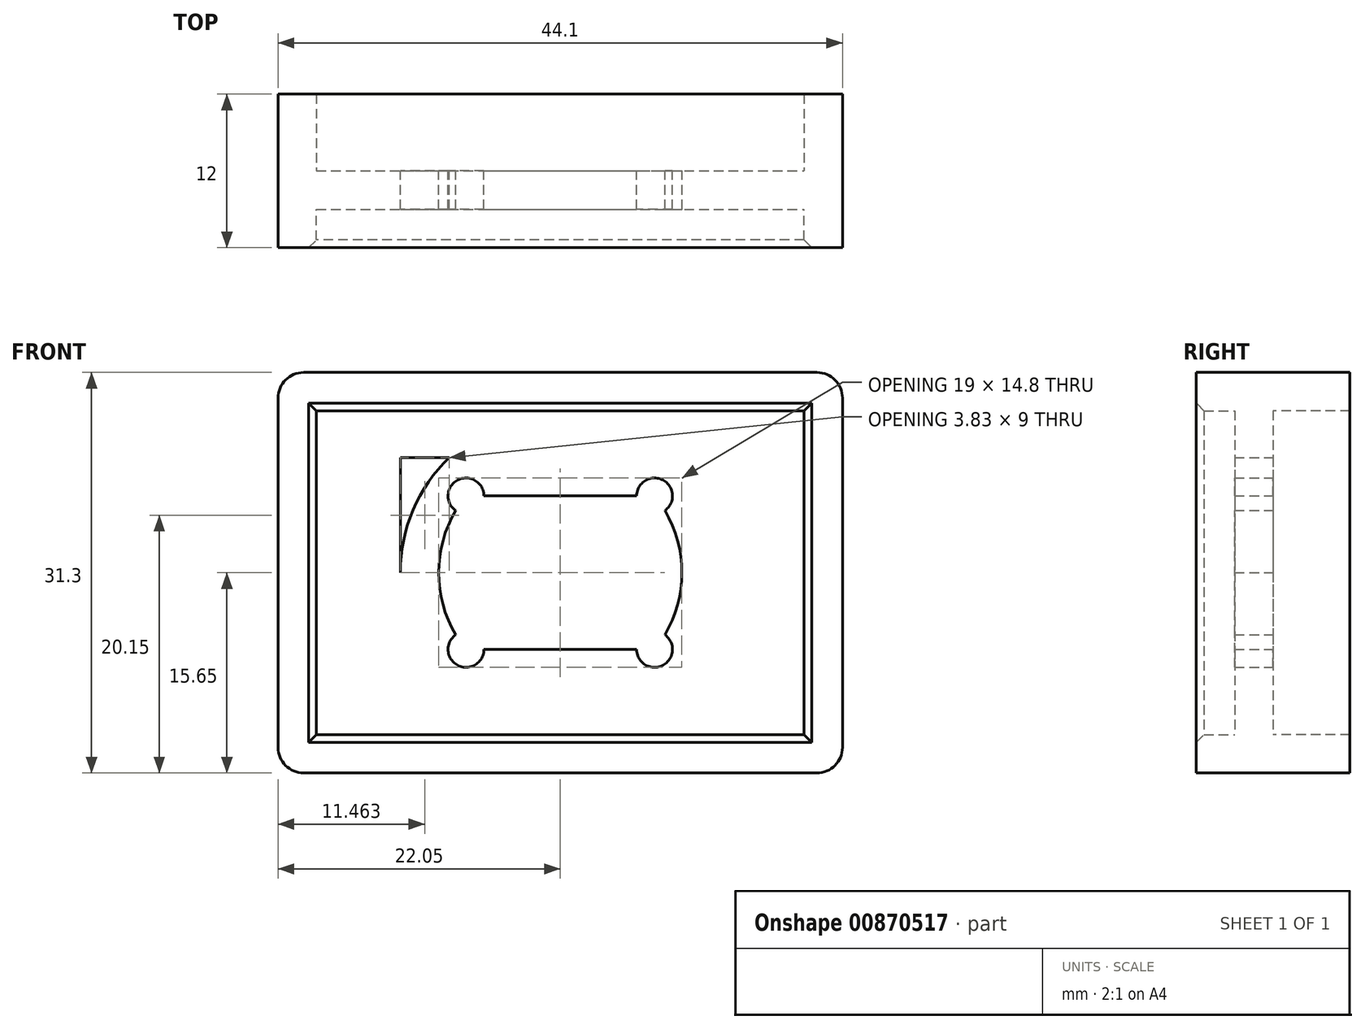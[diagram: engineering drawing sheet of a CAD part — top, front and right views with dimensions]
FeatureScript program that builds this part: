
annotation { "Feature Type Name" : "Feature", "Feature Type Description" : "" }
export const myFeature = defineFeature(function(context is Context, id is Id, definition is map)
    precondition{}
    {
        {
            var Q0;
            Q0=qCreatedBy(makeId("Front.planeOp"),FACE);
            var sketch = newSketch(context, id + "F0", { "sketchPlane" : qUnion([Q0])});
            skLineSegment(sketch, "E0.bottom", {"start": v(-19.05, 12.65) * mm, "end": v(19.05, 12.65) * mm});
            skLineSegment(sketch, "E0.top", {"start": v(-19.05, -12.65) * mm, "end": v(19.05, -12.65) * mm});
            skLineSegment(sketch, "E0.left", {"start": v(-19.05, 12.65) * mm, "end": v(-19.05, -12.65) * mm});
            skLineSegment(sketch, "E0.right", {"start": v(19.05, 12.65) * mm, "end": v(19.05, -12.65) * mm});
            skPoint(sketch, "E0.middle", {"position": v(0, 0) * mm});
            skLineSegment(sketch, "E1.bottom", {"start": v(-22.05, 15.65) * mm, "end": v(22.05, 15.65) * mm});
            skLineSegment(sketch, "E1.top", {"start": v(-22.05, -15.65) * mm, "end": v(22.05, -15.65) * mm});
            skLineSegment(sketch, "E1.left", {"start": v(-22.05, 15.65) * mm, "end": v(-22.05, -15.65) * mm});
            skLineSegment(sketch, "E1.right", {"start": v(22.05, 15.65) * mm, "end": v(22.05, -15.65) * mm});
            skCircle(sketch, "E2", {"center": v(0, 0) * mm, "radius": 9.5 * mm});
            skLineSegment(sketch, "E3.bottom", {"start": v(-9.5, 6) * mm, "end": v(9.5, 6) * mm});
            skLineSegment(sketch, "E3.top", {"start": v(-9.5, -6) * mm, "end": v(9.5, -6) * mm});
            skLineSegment(sketch, "E3.left", {"start": v(-9.5, 6) * mm, "end": v(-9.5, -6) * mm});
            skLineSegment(sketch, "E3.right", {"start": v(9.5, 6) * mm, "end": v(9.5, -6) * mm});
            skCircle(sketch, "E4", {"center": v(0, 0) * mm, "radius": 12.5 * mm});
            skLineSegment(sketch, "E5.bottom", {"start": v(-12.5, 9) * mm, "end": v(12.5, 9) * mm});
            skLineSegment(sketch, "E5.top", {"start": v(-12.5, -9) * mm, "end": v(12.5, -9) * mm});
            skLineSegment(sketch, "E5.left", {"start": v(-12.5, 9) * mm, "end": v(-12.5, -9) * mm});
            skLineSegment(sketch, "E5.right", {"start": v(12.5, 9) * mm, "end": v(12.5, -9) * mm});
            skLineSegment(sketch, "E6.bottom", {"start": v(-7.37, 6) * mm, "end": v(7.37, 6) * mm});
            skLineSegment(sketch, "E6.top", {"start": v(-7.37, -6) * mm, "end": v(7.37, -6) * mm});
            skLineSegment(sketch, "E6.left", {"start": v(-7.37, 6) * mm, "end": v(-7.37, -6) * mm});
            skLineSegment(sketch, "E6.right", {"start": v(7.37, 6) * mm, "end": v(7.37, -6) * mm});
            skCircle(sketch, "E7", {"center": v(-7.37, 6) * mm, "radius": 1.4 * mm});
            skCircle(sketch, "E8", {"center": v(7.37, 6) * mm, "radius": 1.4 * mm});
            skCircle(sketch, "E9", {"center": v(7.37, -6) * mm, "radius": 1.4 * mm});
            skCircle(sketch, "E10", {"center": v(-7.37, -6) * mm, "radius": 1.4 * mm});
            skSolve(sketch);
        }
        {
            var Q0;
            {var subQ0=sQuery(id+"F0.wireOp",EDGE,"diyo5Ijy-Unrl-Ix7s-xjxT-a2Idyrmd7R7O");var subQ1=sQuery(id+"F0.wireOp",EDGE,"E4");var subQ2=makeQuery(id+"F0.imprint","INTERSECT",VERTEX,{"disambiguationData":[OD(0.0)],"derivedFrom":[subQ1,subQ0]});Q0=makeQuery(id+"F0.imprint","IMPRINT",FACE,{"disambiguationData":[TD([[makeQuery(id+"F0.imprint","IMPRINT",EDGE,{"disambiguationData":[TD([[subQ2,-1.0]])],"derivedFrom":subQ1}),1.0]])]});}
            var Q1;
            {var subQ0=sQuery(id+"F0.wireOp",EDGE,"5QQwORZ6-yYhv-RJ5g-prPR-Qrd3KqkXHQQd");var subQ1=sQuery(id+"F0.wireOp",EDGE,"E4");var subQ2=makeQuery(id+"F0.imprint","INTERSECT",VERTEX,{"disambiguationData":[OD(0.0)],"derivedFrom":[subQ1,subQ0]});Q1=makeQuery(id+"F0.imprint","IMPRINT",FACE,{"disambiguationData":[TD([[makeQuery(id+"F0.imprint","IMPRINT",EDGE,{"disambiguationData":[TD([[subQ2,-1.0]])],"derivedFrom":subQ1}),1.0]])]});}
            var Q2;
            Q2=makeQuery(id+"F0.imprint","IMPRINT",FACE,{"disambiguationData":[TD([[makeQuery(id+"F0.imprint","IMPRINT",EDGE,{"derivedFrom":sQuery(id+"F0.wireOp",EDGE,"E0.bottom")}),-1.0]])]});
            var Q3;
            {var subQ0=sQuery(id+"F0.wireOp",EDGE,"E5.bottom");var subQ1=sQuery(id+"F0.wireOp",EDGE,"E2");var subQ2=makeQuery(id+"F0.imprint","INTERSECT",VERTEX,{"disambiguationData":[OD(0.0)],"derivedFrom":[subQ1,subQ0]});Q3=makeQuery(id+"F0.imprint","IMPRINT",FACE,{"disambiguationData":[TD([[makeQuery(id+"F0.imprint","IMPRINT",EDGE,{"disambiguationData":[TD([[subQ2,1.0]])],"derivedFrom":subQ1}),-1.0]])]});}
            var Q4;
            {var subQ0=sQuery(id+"F0.wireOp",EDGE,"RQsxDqyy-hhwE-D28E-GqSd-PO1LcPHCWcnN");var subQ1=sQuery(id+"F0.wireOp",EDGE,"E4");var subQ2=makeQuery(id+"F0.imprint","INTERSECT",VERTEX,{"disambiguationData":[OD(0.0)],"derivedFrom":[subQ1,subQ0]});Q4=makeQuery(id+"F0.imprint","IMPRINT",FACE,{"disambiguationData":[TD([[makeQuery(id+"F0.imprint","IMPRINT",EDGE,{"disambiguationData":[TD([[subQ2,-1.0]])],"derivedFrom":subQ1}),-1.0]])]});}
            var Q5;
            {var subQ0=sQuery(id+"F0.wireOp",EDGE,"E5.right");var subQ1=sQuery(id+"F0.wireOp",EDGE,"E4");var subQ2=makeQuery(id+"F0.imprint","INTERSECT",VERTEX,{"derivedFrom":[subQ1,subQ0]});Q5=makeQuery(id+"F0.imprint","IMPRINT",FACE,{"disambiguationData":[TD([[makeQuery(id+"F0.imprint","IMPRINT",EDGE,{"disambiguationData":[TD([[subQ2,1.0]])],"derivedFrom":subQ1}),-1.0]])]});}
            var Q6;
            {var subQ0=sQuery(id+"F0.wireOp",EDGE,"E5.top");var subQ1=sQuery(id+"F0.wireOp",EDGE,"E2");var subQ2=makeQuery(id+"F0.imprint","INTERSECT",VERTEX,{"disambiguationData":[OD(0.0)],"derivedFrom":[subQ1,subQ0]});Q6=makeQuery(id+"F0.imprint","IMPRINT",FACE,{"disambiguationData":[TD([[makeQuery(id+"F0.imprint","IMPRINT",EDGE,{"disambiguationData":[TD([[subQ2,-1.0]])],"derivedFrom":subQ1}),-1.0]])]});}
            var Q7;
            {var subQ0=sQuery(id+"F0.wireOp",EDGE,"E5.top");var subQ1=sQuery(id+"F0.wireOp",EDGE,"E4");var subQ2=makeQuery(id+"F0.imprint","INTERSECT",VERTEX,{"disambiguationData":[OD(0.0)],"derivedFrom":[subQ1,subQ0]});Q7=makeQuery(id+"F0.imprint","IMPRINT",FACE,{"disambiguationData":[TD([[makeQuery(id+"F0.imprint","IMPRINT",EDGE,{"disambiguationData":[TD([[subQ2,1.0]])],"derivedFrom":subQ1}),-1.0]])]});}
            var Q8;
            {var subQ0=sQuery(id+"F0.wireOp",EDGE,"E5.bottom");var subQ1=sQuery(id+"F0.wireOp",EDGE,"E2");var subQ2=makeQuery(id+"F0.imprint","INTERSECT",VERTEX,{"disambiguationData":[OD(0.0)],"derivedFrom":[subQ1,subQ0]});Q8=makeQuery(id+"F0.imprint","IMPRINT",FACE,{"disambiguationData":[TD([[makeQuery(id+"F0.imprint","IMPRINT",EDGE,{"disambiguationData":[TD([[subQ2,1.0]])],"derivedFrom":subQ1}),1.0]])]});}
            var Q9;
            {var subQ0=sQuery(id+"F0.wireOp",EDGE,"E5.top");var subQ1=sQuery(id+"F0.wireOp",EDGE,"E2");var subQ2=makeQuery(id+"F0.imprint","INTERSECT",VERTEX,{"disambiguationData":[OD(0.0)],"derivedFrom":[subQ1,subQ0]});Q9=makeQuery(id+"F0.imprint","IMPRINT",FACE,{"disambiguationData":[TD([[makeQuery(id+"F0.imprint","IMPRINT",EDGE,{"disambiguationData":[TD([[subQ2,-1.0]])],"derivedFrom":subQ1}),1.0]])]});}
            var Q10;
            {var subQ0=sQuery(id+"F0.wireOp",EDGE,"diyo5Ijy-Unrl-Ix7s-xjxT-a2Idyrmd7R7O");var subQ1=sQuery(id+"F0.wireOp",EDGE,"E4");var subQ2=makeQuery(id+"F0.imprint","INTERSECT",VERTEX,{"disambiguationData":[OD(1.0)],"derivedFrom":[subQ1,subQ0]});Q10=makeQuery(id+"F0.imprint","IMPRINT",FACE,{"disambiguationData":[TD([[makeQuery(id+"F0.imprint","IMPRINT",EDGE,{"disambiguationData":[TD([[subQ2,-1.0]])],"derivedFrom":subQ1}),-1.0]])]});}
            var Q11;
            {var subQ1=sQuery(id+"F0.wireOp",EDGE,"E2");var subQ6=sQuery(id+"F0.wireOp",EDGE,"E5.bottom");var subQ14=makeQuery(id+"F0.imprint","INTERSECT",VERTEX,{"disambiguationData":[OD(0.0)],"derivedFrom":[subQ1,subQ6]});Q11=makeQuery(id+"F0.imprint","IMPRINT",FACE,{"disambiguationData":[TD([[makeQuery(id+"F0.imprint","IMPRINT",EDGE,{"disambiguationData":[TD([[subQ14,-1.0]])],"derivedFrom":subQ1}),-1.0]])]});}
            var Q12;
            {var subQ0=sQuery(id+"F0.wireOp",EDGE,"diyo5Ijy-Unrl-Ix7s-xjxT-a2Idyrmd7R7O");var subQ1=sQuery(id+"F0.wireOp",EDGE,"E4");var subQ2=makeQuery(id+"F0.imprint","INTERSECT",VERTEX,{"disambiguationData":[OD(0.0)],"derivedFrom":[subQ1,subQ0]});Q12=makeQuery(id+"F0.imprint","IMPRINT",FACE,{"disambiguationData":[TD([[makeQuery(id+"F0.imprint","IMPRINT",EDGE,{"disambiguationData":[TD([[subQ2,-1.0]])],"derivedFrom":subQ1}),-1.0]])]});}
            var Q13;
            {var subQ0=sQuery(id+"F0.wireOp",EDGE,"RQsxDqyy-hhwE-D28E-GqSd-PO1LcPHCWcnN");var subQ1=sQuery(id+"F0.wireOp",EDGE,"E4");var subQ2=makeQuery(id+"F0.imprint","INTERSECT",VERTEX,{"disambiguationData":[OD(0.0)],"derivedFrom":[subQ1,subQ0]});Q13=makeQuery(id+"F0.imprint","IMPRINT",FACE,{"disambiguationData":[TD([[makeQuery(id+"F0.imprint","IMPRINT",EDGE,{"disambiguationData":[TD([[subQ2,1.0]])],"derivedFrom":subQ1}),-1.0]])]});}
            var Q14;
            {var subQ0=sQuery(id+"F0.wireOp",EDGE,"5QQwORZ6-yYhv-RJ5g-prPR-Qrd3KqkXHQQd");var subQ1=sQuery(id+"F0.wireOp",EDGE,"E4");var subQ2=makeQuery(id+"F0.imprint","INTERSECT",VERTEX,{"disambiguationData":[OD(0.0)],"derivedFrom":[subQ1,subQ0]});Q14=makeQuery(id+"F0.imprint","IMPRINT",FACE,{"disambiguationData":[TD([[makeQuery(id+"F0.imprint","IMPRINT",EDGE,{"disambiguationData":[TD([[subQ2,-1.0]])],"derivedFrom":subQ1}),-1.0]])]});}
            var Q15;
            {var subQ0=sQuery(id+"F0.wireOp",EDGE,"Sn6az9JK-Su7q-VoNe-VHIh-EGGie5zRdxJw");var subQ1=sQuery(id+"F0.wireOp",EDGE,"E4");var subQ2=makeQuery(id+"F0.imprint","INTERSECT",VERTEX,{"disambiguationData":[OD(0.0)],"derivedFrom":[subQ1,subQ0]});Q15=makeQuery(id+"F0.imprint","IMPRINT",FACE,{"disambiguationData":[TD([[makeQuery(id+"F0.imprint","IMPRINT",EDGE,{"disambiguationData":[TD([[subQ2,-1.0]])],"derivedFrom":subQ1}),-1.0]])]});}
            var Q16;
            {var subQ1=sQuery(id+"F0.wireOp",EDGE,"E2");var subQ6=sQuery(id+"F0.wireOp",EDGE,"E5.bottom");var subQ14=makeQuery(id+"F0.imprint","INTERSECT",VERTEX,{"disambiguationData":[OD(0.0)],"derivedFrom":[subQ1,subQ6]});Q16=makeQuery(id+"F0.imprint","IMPRINT",FACE,{"disambiguationData":[TD([[makeQuery(id+"F0.imprint","IMPRINT",EDGE,{"disambiguationData":[TD([[subQ14,-1.0]])],"derivedFrom":subQ1}),-1.0]])]});}
            var Q17;
            {var subQ1=sQuery(id+"F0.wireOp",EDGE,"E2");var subQ13=sQuery(id+"F0.wireOp",EDGE,"E9");var subQ14=makeQuery(id+"F0.imprint","INTERSECT",VERTEX,{"disambiguationData":[OD(0.0)],"derivedFrom":[subQ1,subQ13]});Q17=makeQuery(id+"F0.imprint","IMPRINT",FACE,{"disambiguationData":[TD([[makeQuery(id+"F0.imprint","IMPRINT",EDGE,{"disambiguationData":[TD([[subQ14,1.0]])],"derivedFrom":subQ1}),-1.0]])]});}
            var Q18;
            {var subQ1=sQuery(id+"F0.wireOp",EDGE,"E2");var subQ13=sQuery(id+"F0.wireOp",EDGE,"E9");var subQ14=makeQuery(id+"F0.imprint","INTERSECT",VERTEX,{"disambiguationData":[OD(0.0)],"derivedFrom":[subQ1,subQ13]});Q18=makeQuery(id+"F0.imprint","IMPRINT",FACE,{"disambiguationData":[TD([[makeQuery(id+"F0.imprint","IMPRINT",EDGE,{"disambiguationData":[TD([[subQ14,1.0]])],"derivedFrom":subQ1}),-1.0]])]});}
            var Q19;
            {var subQ0=sQuery(id+"F0.wireOp",EDGE,"E9");var subQ1=sQuery(id+"F0.wireOp",EDGE,"E2");var subQ2=makeQuery(id+"F0.imprint","INTERSECT",VERTEX,{"disambiguationData":[OD(1.0)],"derivedFrom":[subQ1,subQ0]});Q19=makeQuery(id+"F0.imprint","IMPRINT",FACE,{"disambiguationData":[TD([[makeQuery(id+"F0.imprint","IMPRINT",EDGE,{"disambiguationData":[TD([[subQ2,-1.0]])],"derivedFrom":subQ1}),-1.0]])]});}
            var Q20;
            {var subQ0=sQuery(id+"F0.wireOp",EDGE,"E3.left");var subQ1=sQuery(id+"F0.wireOp",EDGE,"E2");var subQ2=makeQuery(id+"F0.imprint","INTERSECT",VERTEX,{"derivedFrom":[subQ1,subQ0]});Q20=makeQuery(id+"F0.imprint","IMPRINT",FACE,{"disambiguationData":[TD([[makeQuery(id+"F0.imprint","IMPRINT",EDGE,{"disambiguationData":[TD([[subQ2,-1.0]])],"derivedFrom":subQ1}),-1.0]])]});}
            var Q21;
            {var subQ0=sQuery(id+"F0.wireOp",EDGE,"E7");var subQ1=sQuery(id+"F0.wireOp",EDGE,"E2");var subQ2=makeQuery(id+"F0.imprint","INTERSECT",VERTEX,{"disambiguationData":[OD(1.0)],"derivedFrom":[subQ1,subQ0]});Q21=makeQuery(id+"F0.imprint","IMPRINT",FACE,{"disambiguationData":[TD([[makeQuery(id+"F0.imprint","IMPRINT",EDGE,{"disambiguationData":[TD([[subQ2,-1.0]])],"derivedFrom":subQ1}),-1.0]])]});}
            var Q22;
            {var subQ0=sQuery(id+"F0.wireOp",EDGE,"E3.right");var subQ1=sQuery(id+"F0.wireOp",EDGE,"E2");var subQ2=makeQuery(id+"F0.imprint","INTERSECT",VERTEX,{"derivedFrom":[subQ1,subQ0]});Q22=makeQuery(id+"F0.imprint","IMPRINT",FACE,{"disambiguationData":[TD([[makeQuery(id+"F0.imprint","IMPRINT",EDGE,{"disambiguationData":[TD([[subQ2,-1.0]])],"derivedFrom":subQ1}),-1.0]])]});}
            var Q23;
            {var subQ0=sQuery(id+"F0.wireOp",EDGE,"E3.left");var subQ1=sQuery(id+"F0.wireOp",EDGE,"E2");var subQ2=makeQuery(id+"F0.imprint","INTERSECT",VERTEX,{"derivedFrom":[subQ1,subQ0]});Q23=makeQuery(id+"F0.imprint","IMPRINT",FACE,{"disambiguationData":[TD([[makeQuery(id+"F0.imprint","IMPRINT",EDGE,{"disambiguationData":[TD([[subQ2,-1.0]])],"derivedFrom":subQ1}),-1.0]])]});}
            var Q24;
            {var subQ0=sQuery(id+"F0.wireOp",EDGE,"E9");var subQ1=sQuery(id+"F0.wireOp",EDGE,"E2");var subQ2=makeQuery(id+"F0.imprint","INTERSECT",VERTEX,{"disambiguationData":[OD(1.0)],"derivedFrom":[subQ1,subQ0]});Q24=makeQuery(id+"F0.imprint","IMPRINT",FACE,{"disambiguationData":[TD([[makeQuery(id+"F0.imprint","IMPRINT",EDGE,{"disambiguationData":[TD([[subQ2,-1.0]])],"derivedFrom":subQ1}),-1.0]])]});}
            var Q25;
            {var subQ0=sQuery(id+"F0.wireOp",EDGE,"E7");var subQ1=sQuery(id+"F0.wireOp",EDGE,"E4");var subQ2=makeQuery(id+"F0.imprint","INTERSECT",VERTEX,{"disambiguationData":[OD(1.0)],"derivedFrom":[subQ1,subQ0]});Q25=makeQuery(id+"F0.imprint","IMPRINT",FACE,{"disambiguationData":[TD([[makeQuery(id+"F0.imprint","IMPRINT",EDGE,{"disambiguationData":[TD([[subQ2,-1.0]])],"derivedFrom":subQ1}),-1.0]])]});}
            var Q26;
            {var subQ0=sQuery(id+"F0.wireOp",EDGE,"E8");var subQ1=sQuery(id+"F0.wireOp",EDGE,"E4");var subQ2=makeQuery(id+"F0.imprint","INTERSECT",VERTEX,{"disambiguationData":[OD(0.0)],"derivedFrom":[subQ1,subQ0]});Q26=makeQuery(id+"F0.imprint","IMPRINT",FACE,{"disambiguationData":[TD([[makeQuery(id+"F0.imprint","IMPRINT",EDGE,{"disambiguationData":[TD([[subQ2,1.0]])],"derivedFrom":subQ1}),-1.0]])]});}
            var Q27;
            {var subQ0=sQuery(id+"F0.wireOp",EDGE,"E5.bottom");var subQ1=sQuery(id+"F0.wireOp",EDGE,"E4");var subQ2=makeQuery(id+"F0.imprint","INTERSECT",VERTEX,{"disambiguationData":[OD(0.0)],"derivedFrom":[subQ1,subQ0]});Q27=makeQuery(id+"F0.imprint","IMPRINT",FACE,{"disambiguationData":[TD([[makeQuery(id+"F0.imprint","IMPRINT",EDGE,{"disambiguationData":[TD([[subQ2,-1.0]])],"derivedFrom":subQ1}),-1.0]])]});}
            var Q28;
            {var subQ0=sQuery(id+"F0.wireOp",EDGE,"E5.right");var subQ1=sQuery(id+"F0.wireOp",EDGE,"E4");var subQ2=makeQuery(id+"F0.imprint","INTERSECT",VERTEX,{"derivedFrom":[subQ1,subQ0]});Q28=makeQuery(id+"F0.imprint","IMPRINT",FACE,{"disambiguationData":[TD([[makeQuery(id+"F0.imprint","IMPRINT",EDGE,{"disambiguationData":[TD([[subQ2,-1.0]])],"derivedFrom":subQ1}),-1.0]])]});}
            var Q29;
            {var subQ3=sQuery(id+"F0.wireOp",EDGE,"E8");var subQ5=sQuery(id+"F0.wireOp",EDGE,"E2");var subQ6=makeQuery(id+"F0.imprint","INTERSECT",VERTEX,{"disambiguationData":[OD(1.0)],"derivedFrom":[subQ5,subQ3]});Q29=makeQuery(id+"F0.imprint","IMPRINT",FACE,{"disambiguationData":[TD([[makeQuery(id+"F0.imprint","IMPRINT",EDGE,{"disambiguationData":[TD([[subQ6,-1.0]])],"derivedFrom":subQ5}),1.0]])]});}
            var Q30;
            {var subQ1=sQuery(id+"F0.wireOp",EDGE,"E2");var subQ7=sQuery(id+"F0.wireOp",EDGE,"E9");var subQ10=makeQuery(id+"F0.imprint","INTERSECT",VERTEX,{"disambiguationData":[OD(0.0)],"derivedFrom":[subQ1,subQ7]});Q30=makeQuery(id+"F0.imprint","IMPRINT",FACE,{"disambiguationData":[TD([[makeQuery(id+"F0.imprint","IMPRINT",EDGE,{"disambiguationData":[TD([[subQ10,1.0]])],"derivedFrom":subQ1}),1.0]])]});}
            extrude(context, id + "F1", {"entities" : qUnion([Q0, Q1, Q2, Q3, Q4, Q5, Q6, Q7, Q8, Q9, Q10, Q11, Q12, Q13, Q14, Q15, Q16, Q17, Q18, Q19, Q20, Q21, Q22, Q23, Q24, Q25, Q26, Q27, Q28, Q29, Q30]), "depth" : 3 * mm, "offsetDistance" : 25 * mm});
        }
        {
            var Q0;
            Q0=makeQuery(id+"F0.imprint","IMPRINT",FACE,{"disambiguationData":[TD([[makeQuery(id+"F0.imprint","IMPRINT",EDGE,{"derivedFrom":sQuery(id+"F0.wireOp",EDGE,"E0.bottom")}),1.0]])]});
            extrude(context, id + "F2", {"entities" : qUnion([Q0]), "operationType" : NewBodyOperationType.ADD, "depth" : 6 * mm, "offsetDistance" : 25 * mm});
        }
        {
            var Q0;
            Q0=makeQuery(id+"F0.imprint","IMPRINT",FACE,{"disambiguationData":[TD([[makeQuery(id+"F0.imprint","IMPRINT",EDGE,{"derivedFrom":sQuery(id+"F0.wireOp",EDGE,"E0.bottom")}),1.0]])]});
            extrude(context, id + "F3", {"entities" : qUnion([Q0]), "operationType" : NewBodyOperationType.ADD, "oppositeDirection" : true, "depth" : 6 * mm, "offsetDistance" : 25 * mm});
        }
        {
            var Q0;
            Q0=makeQuery(id+"F2.opExtrude","CAP_EDGE",EDGE,{"disambiguationData":[OSD([sQuery(id+"F0.wireOp",EDGE,"E0.left")])],"isStart":false});
            var Q1;
            Q1=makeQuery(id+"F2.opExtrude","CAP_EDGE",EDGE,{"disambiguationData":[OSD([sQuery(id+"F0.wireOp",EDGE,"E0.top")])],"isStart":false});
            var Q2;
            Q2=makeQuery(id+"F2.opExtrude","CAP_EDGE",EDGE,{"disambiguationData":[OSD([sQuery(id+"F0.wireOp",EDGE,"E0.bottom")])],"isStart":false});
            var Q3;
            Q3=makeQuery(id+"F2.opExtrude","CAP_EDGE",EDGE,{"disambiguationData":[OSD([sQuery(id+"F0.wireOp",EDGE,"E0.right")])],"isStart":false});
            chamfer(context, id + "F4", {"entities" : qUnion([Q0, Q1, Q2, Q3]), "width" : 0.6 * mm, "tangentPropagation" : true});
        }
        {
            var Q0;
            {var subQ0=sQuery(id+"F0.wireOp",EDGE,"E1.right");var subQ1=sQuery(id+"F0.wireOp",EDGE,"E1.bottom");Q0=makeQuery(id+"F3.boolean.opBoolean","MERGE",EDGE,{"derivedFrom":[makeQuery(id+"F2.opExtrude","SWEPT_EDGE",EDGE,{"disambiguationData":[OSD([subQ1,subQ0])]}),makeQuery(id+"F3.opExtrude","SWEPT_EDGE",EDGE,{"disambiguationData":[OSD([subQ1,subQ0])]})]});}
            var Q1;
            {var subQ0=sQuery(id+"F0.wireOp",EDGE,"E1.right");var subQ1=sQuery(id+"F0.wireOp",EDGE,"E1.top");Q1=makeQuery(id+"F3.boolean.opBoolean","MERGE",EDGE,{"derivedFrom":[makeQuery(id+"F2.opExtrude","SWEPT_EDGE",EDGE,{"disambiguationData":[OSD([subQ1,subQ0])]}),makeQuery(id+"F3.opExtrude","SWEPT_EDGE",EDGE,{"disambiguationData":[OSD([subQ1,subQ0])]})]});}
            var Q2;
            {var subQ0=sQuery(id+"F0.wireOp",EDGE,"E1.left");var subQ1=sQuery(id+"F0.wireOp",EDGE,"E1.top");Q2=makeQuery(id+"F3.boolean.opBoolean","MERGE",EDGE,{"derivedFrom":[makeQuery(id+"F2.opExtrude","SWEPT_EDGE",EDGE,{"disambiguationData":[OSD([subQ1,subQ0])]}),makeQuery(id+"F3.opExtrude","SWEPT_EDGE",EDGE,{"disambiguationData":[OSD([subQ1,subQ0])]})]});}
            var Q3;
            {var subQ0=sQuery(id+"F0.wireOp",EDGE,"E1.left");var subQ1=sQuery(id+"F0.wireOp",EDGE,"E1.bottom");Q3=makeQuery(id+"F3.boolean.opBoolean","MERGE",EDGE,{"derivedFrom":[makeQuery(id+"F2.opExtrude","SWEPT_EDGE",EDGE,{"disambiguationData":[OSD([subQ1,subQ0])]}),makeQuery(id+"F3.opExtrude","SWEPT_EDGE",EDGE,{"disambiguationData":[OSD([subQ1,subQ0])]})]});}
            fillet(context, id + "F5", {"entities" : qUnion([Q0, Q1, Q2, Q3]), "radius" : 2 * mm, "tangentPropagation" : true, "allowEdgeOverflow" : false});
        }
    });
